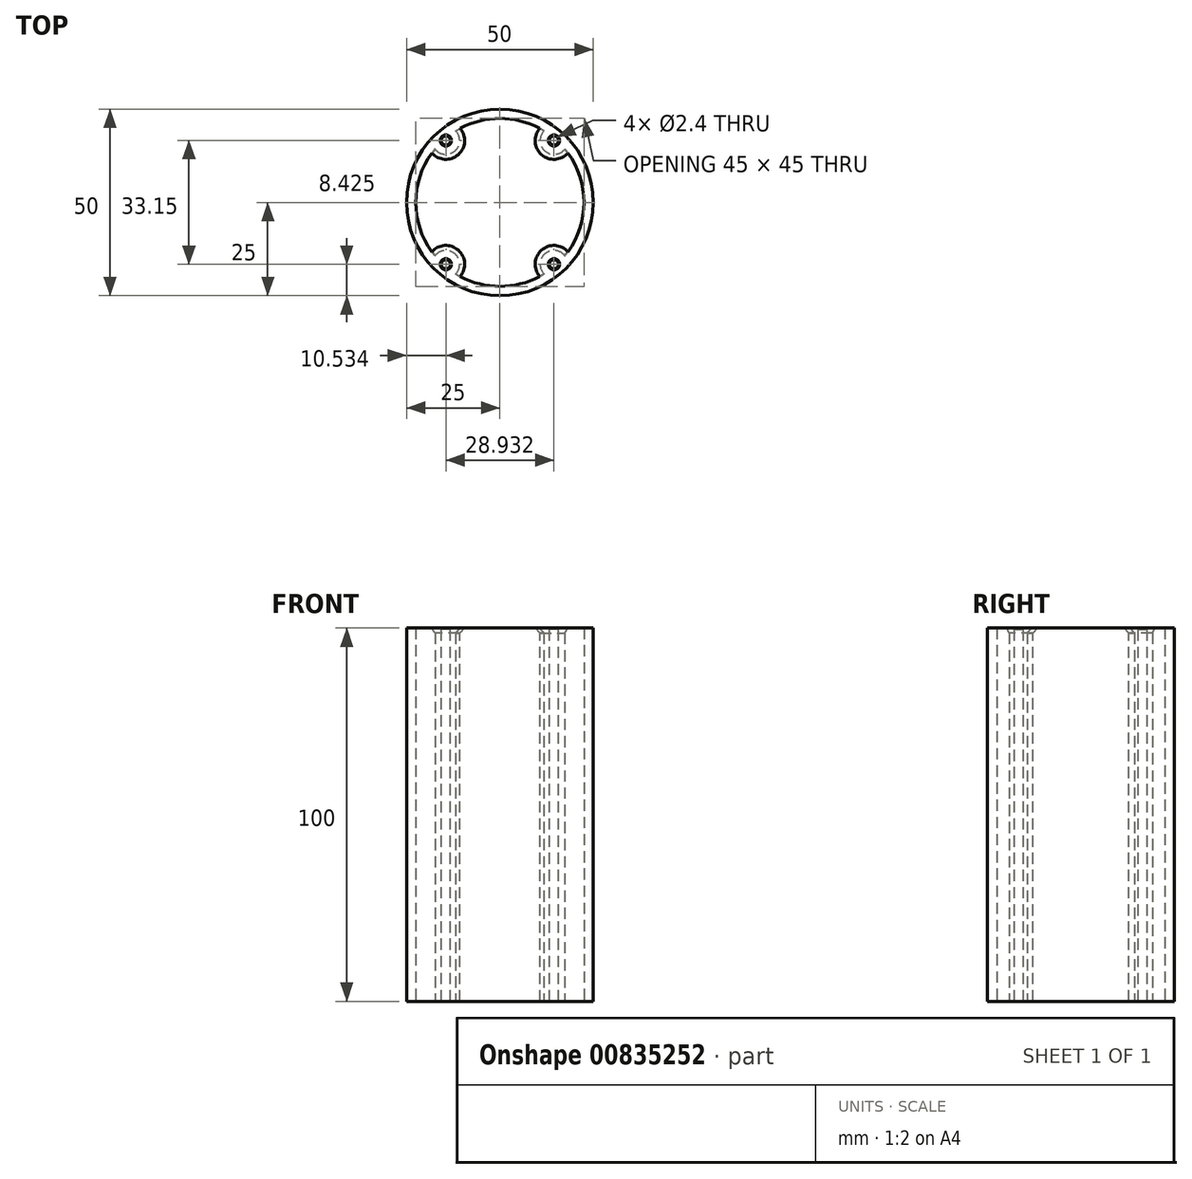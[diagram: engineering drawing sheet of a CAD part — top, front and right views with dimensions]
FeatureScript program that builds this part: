
annotation { "Feature Type Name" : "Feature", "Feature Type Description" : "" }
export const myFeature = defineFeature(function(context is Context, id is Id, definition is map)
    precondition{}
    {
        {
            var Q0;
            Q0=qCreatedBy(makeId("Top.planeOp"),FACE);
            var sketch = newSketch(context, id + "F0", { "sketchPlane" : qUnion([Q0])});
            skCircle(sketch, "E0", {"center": v(0, 0) * mm, "radius": 25 * mm});
            skSolve(sketch);
        }
        {
            var Q0;
            Q0=makeQuery(id+"F0.imprint","IMPRINT",FACE,{"disambiguationData":[TD([[makeQuery(id+"F0.imprint","IMPRINT",EDGE,{"derivedFrom":sQuery(id+"F0.wireOp",EDGE,"E0")}),1.0]])]});
            extrude(context, id + "F1", {"entities" : qUnion([Q0]), "depth" : 100 * mm, "offsetDistance" : 25 * mm});
        }
        {
            var Q0;
            Q0=makeQuery(id+"F1.opExtrude","CAP_FACE",FACE,{"disambiguationData":[OSD([sQuery(id+"F0.wireOp",EDGE,"E0")])],"isStart":false});
            var sketch = newSketch(context, id + "F2", { "sketchPlane" : qUnion([Q0])});
            skCircle(sketch, "E1", {"center": v(-14.47, -16.57) * mm, "radius": 3 * mm});
            skPoint(sketch, "E1.first.point", {"position": v(-16.44, -18.84) * mm});
            skPoint(sketch, "E1.second.point", {"position": v(-12.8, -14.08) * mm});
            skPoint(sketch, "E1.third.point", {"position": v(-15.23, -13.67) * mm});
            skCircle(sketch, "E2", {"center": v(-14.47, -16.57) * mm, "radius": 1.25 * mm});
            skCircle(sketch, "E3.MirrorC", {"center": v(-14.47, 16.57) * mm, "radius": 1.25 * mm});
            skCircle(sketch, "E4.MirrorC", {"center": v(-14.47, 16.57) * mm, "radius": 3 * mm});
            skCircle(sketch, "E5.MirrorC", {"center": v(14.47, -16.57) * mm, "radius": 1.25 * mm});
            skCircle(sketch, "E6.MirrorC", {"center": v(14.47, -16.57) * mm, "radius": 3 * mm});
            skCircle(sketch, "E7.MirrorC", {"center": v(14.47, 16.57) * mm, "radius": 3 * mm});
            skCircle(sketch, "E8.MirrorC", {"center": v(14.47, 16.57) * mm, "radius": 1.25 * mm});
            skSolve(sketch);
        }
        {
            var Q0;
            Q0=sQuery(id+"F2.wireOp",VERTEX,"E7.MirrorC.center");
            var Q1;
            Q1=sQuery(id+"F2.wireOp",VERTEX,"E5.MirrorC.center");
            var Q2;
            Q2=sQuery(id+"F2.wireOp",VERTEX,"E1.center");
            var Q3;
            Q3=sQuery(id+"F2.wireOp",VERTEX,"E3.MirrorC.center");
            var Q4;
            Q4=makeQuery(id+"F1.opExtrude","SWEPT_BODY",BODY,{"disambiguationData":[OSD([sQuery(id+"F0.wireOp",EDGE,"E0")])]});
            hole(context, id + "F3", {"style" : HoleStyle.C_SINK, "endStyle" : HoleEndStyle.THROUGH, "holeDiameter" : 2.4 * mm, "cSinkDiameter" : 3 * mm, "cSinkAngle" : 90 * degree, "majorDiameter" : 5 * mm, "isTappedThrough" : true, "tappedDepth" : 12 * mm, "tapClearance" : 3, "locations" : qUnion([Q0, Q1, Q2, Q3]), "scope" : qUnion([Q4])});
        }
        {
            var Q0;
            Q0=makeQuery(id+"F1.opExtrude","CAP_FACE",FACE,{"disambiguationData":[OSD([sQuery(id+"F0.wireOp",EDGE,"E0")])],"isStart":true});
            var Q1;
            Q1=makeQuery(id+"F1.opExtrude","CAP_FACE",FACE,{"disambiguationData":[OSD([sQuery(id+"F0.wireOp",EDGE,"E0")])],"isStart":false});
            shell(context, id + "F4", {"entities" : qUnion([Q0, Q1]), "thickness" : 2.5 * mm});
        }
    });
